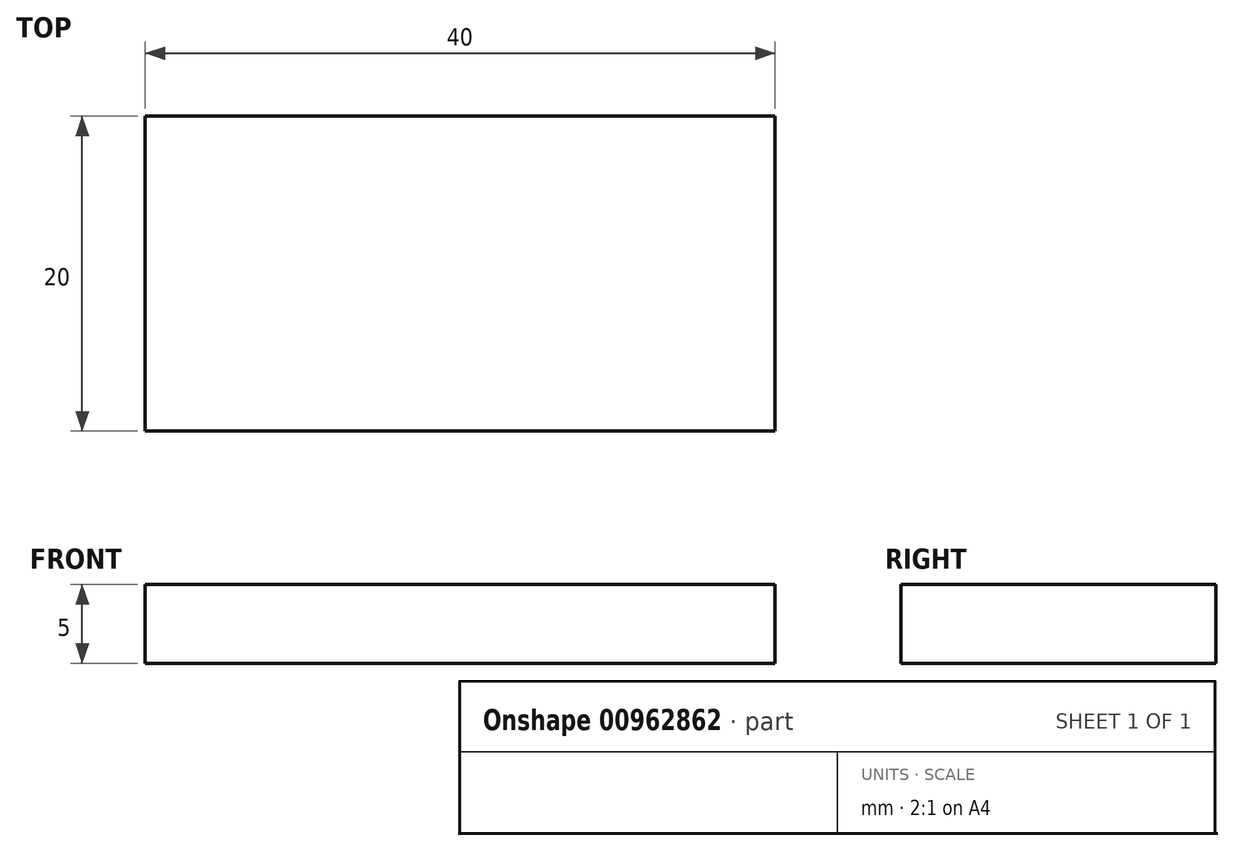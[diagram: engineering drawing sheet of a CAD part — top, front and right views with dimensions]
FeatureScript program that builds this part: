
annotation { "Feature Type Name" : "Feature", "Feature Type Description" : "" }
export const myFeature = defineFeature(function(context is Context, id is Id, definition is map)
    precondition{}
    {
        {
            var Q0;
            Q0=qCreatedBy(makeId("Top.planeOp"),FACE);
            var sketch = newSketch(context, id + "F0", { "sketchPlane" : qUnion([Q0])});
            skLineSegment(sketch, "E0.bottom", {"start": v(20, 10) * mm, "end": v(-20, 10) * mm});
            skLineSegment(sketch, "E0.top", {"start": v(20, -10) * mm, "end": v(-20, -10) * mm});
            skLineSegment(sketch, "E0.left", {"start": v(20, 10) * mm, "end": v(20, -10) * mm});
            skLineSegment(sketch, "E0.right", {"start": v(-20, 10) * mm, "end": v(-20, -10) * mm});
            skPoint(sketch, "E0.middle", {"position": v(0, 0) * mm});
            skSolve(sketch);
        }
        {
            var Q0;
            Q0 = qSketchRegion(id + "F0", true);
            extrude(context, id + "F1", {"entities" : qUnion([Q0]), "depth" : 5 * mm, "offsetDistance" : 25 * mm});
        }
    });
